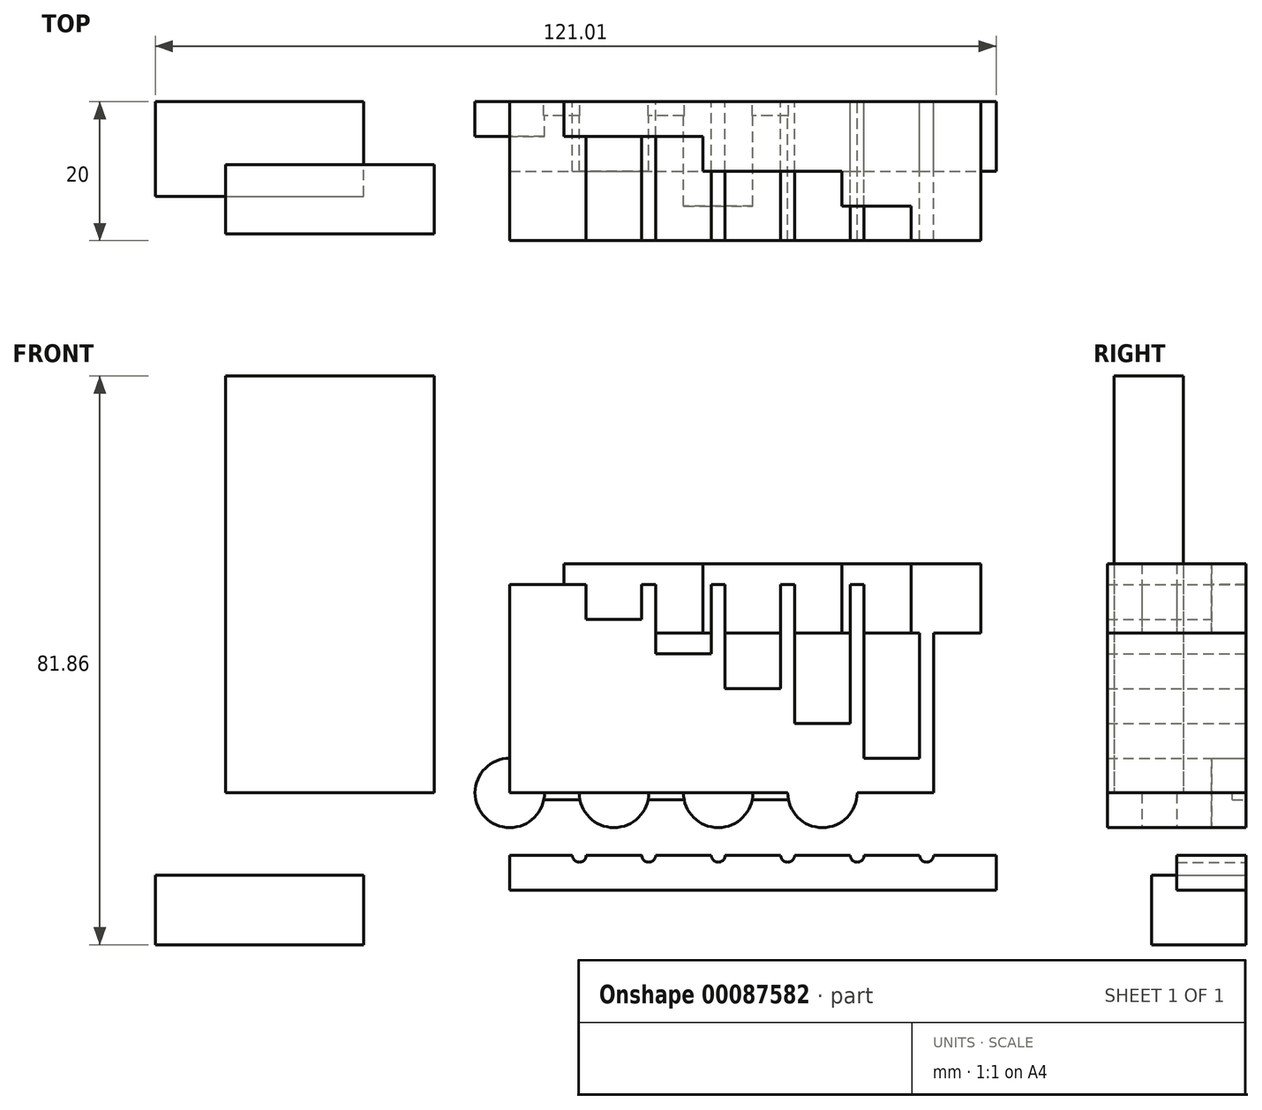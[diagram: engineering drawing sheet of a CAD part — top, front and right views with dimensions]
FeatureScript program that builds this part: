
annotation { "Feature Type Name" : "Feature", "Feature Type Description" : "" }
export const myFeature = defineFeature(function(context is Context, id is Id, definition is map)
    precondition{}
    {
        {
            var Q0;
            Q0=qCreatedBy(makeId("Front.planeOp"),FACE);
            var sketch = newSketch(context, id + "F0", { "sketchPlane" : qUnion([Q0])});
            skCircle(sketch, "E0", {"center": v(0, 0) * mm, "radius": 5 * mm});
            skCircle(sketch, "E1.1.0.0", {"center": v(15, 0) * mm, "radius": 5 * mm});
            skCircle(sketch, "E1.2.0.0", {"center": v(30, 0) * mm, "radius": 5 * mm});
            skCircle(sketch, "E1.3.0.0", {"center": v(45, 0) * mm, "radius": 5 * mm});
            skLineSegment(sketch, "E1.direction1", {"start": v(0, 0) * mm, "end": v(15, 0) * mm, "construction": true});
            skSolve(sketch);
        }
        {
            var Q0;
            Q0=makeQuery(id+"F0.imprint","IMPRINT",FACE,{"disambiguationData":[TD([[makeQuery(id+"F0.imprint","IMPRINT",EDGE,{"derivedFrom":sQuery(id+"F0.wireOp",EDGE,"E0")}),1.0]])]});
            extrude(context, id + "F1", {"entities" : qUnion([Q0]), "depth" : 5 * mm});
        }
        {
            var Q0;
            Q0=makeQuery(id+"F0.imprint","IMPRINT",FACE,{"disambiguationData":[TD([[makeQuery(id+"F0.imprint","IMPRINT",EDGE,{"derivedFrom":sQuery(id+"F0.wireOp",EDGE,"E1.1.0.0")}),1.0]])]});
            extrude(context, id + "F2", {"entities" : qUnion([Q0]), "depth" : 10 * mm});
        }
        {
            var Q0;
            Q0=makeQuery(id+"F0.imprint","IMPRINT",FACE,{"disambiguationData":[TD([[makeQuery(id+"F0.imprint","IMPRINT",EDGE,{"derivedFrom":sQuery(id+"F0.wireOp",EDGE,"E1.2.0.0")}),1.0]])]});
            extrude(context, id + "F3", {"entities" : qUnion([Q0]), "depth" : 15 * mm});
        }
        {
            var Q0;
            Q0=makeQuery(id+"F0.imprint","IMPRINT",FACE,{"disambiguationData":[TD([[makeQuery(id+"F0.imprint","IMPRINT",EDGE,{"derivedFrom":sQuery(id+"F0.wireOp",EDGE,"E1.3.0.0")}),1.0]])]});
            extrude(context, id + "F4", {"entities" : qUnion([Q0]), "depth" : 20 * mm});
        }
        {
            var Q0;
            Q0=makeQuery(id+"F0.imprint","IMPRINT",FACE,{"disambiguationData":[TD([[makeQuery(id+"F0.imprint","IMPRINT",EDGE,{"derivedFrom":sQuery(id+"F0.wireOp",EDGE,"E0")}),1.0]])]});
            var sketch = newSketch(context, id + "F5", { "sketchPlane" : qUnion([Q0])});
            skArc(sketch, "E2.0", {"start": v(45, -5) * mm, "mid": v(50, 0) * mm, "end": v(45, 5) * mm});
            skArc(sketch, "E2.1", {"start": v(0, 5) * mm, "mid": v(-5, 0) * mm, "end": v(0, -5) * mm});
            skLineSegment(sketch, "E3", {"start": v(45, -5) * mm, "end": v(0, -5) * mm});
            skLineSegment(sketch, "E4", {"start": v(0, 5) * mm, "end": v(45, 5) * mm});
            skSolve(sketch);
        }
        {
            var Q0;
            Q0=makeQuery(id+"F4.opExtrude","SWEPT_BODY",BODY,{"disambiguationData":[OSD([sQuery(id+"F0.wireOp",EDGE,"E1.3.0.0")])]});
            var Q1;
            Q1=makeQuery(id+"FrmGR7nz3px04QZ_4.opExtrude","SWEPT_BODY",BODY,{"disambiguationData":[OSD([sQuery(id+"F5.wireOp",EDGE,"E2.0"),sQuery(id+"F5.wireOp",EDGE,"E2.1"),sQuery(id+"F5.wireOp",EDGE,"E3"),sQuery(id+"F5.wireOp",EDGE,"E4")])]});
            var Q2;
            Q2=makeQuery(id+"F3.opExtrude","SWEPT_BODY",BODY,{"disambiguationData":[OSD([sQuery(id+"F0.wireOp",EDGE,"E1.2.0.0")])]});
            var Q3;
            Q3=makeQuery(id+"F2.opExtrude","SWEPT_BODY",BODY,{"disambiguationData":[OSD([sQuery(id+"F0.wireOp",EDGE,"E1.1.0.0")])]});
            var Q4;
            Q4=makeQuery(id+"F1.opExtrude","SWEPT_BODY",BODY,{"disambiguationData":[OSD([sQuery(id+"F0.wireOp",EDGE,"E0")])]});
            booleanBodies(context, id + "F6", {"operationType" : BooleanOperationType.UNION, "tools" : qUnion([Q0, Q1, Q2, Q3, Q4])});
        }
        {
            var Q0;
            Q0=makeQuery(id+"F6.opBoolean","MERGE",FACE,{"derivedFrom":[makeQuery(id+"F4.opExtrude","CAP_FACE",FACE,{"disambiguationData":[OSD([sQuery(id+"F0.wireOp",EDGE,"E1.3.0.0")])],"isStart":true}),makeQuery(id+"FrmGR7nz3px04QZ_4.opExtrude","CAP_FACE",FACE,{"disambiguationData":[OSD([sQuery(id+"F5.wireOp",EDGE,"E2.0"),sQuery(id+"F5.wireOp",EDGE,"E2.1"),sQuery(id+"F5.wireOp",EDGE,"E3"),sQuery(id+"F5.wireOp",EDGE,"E4")])],"isStart":true})]});
            var sketch = newSketch(context, id + "F7", { "sketchPlane" : qUnion([Q0])});
            skLineSegment(sketch, "E5.bottom", {"start": v(-67.8, 23) * mm, "end": v(-7.8, 23) * mm});
            skLineSegment(sketch, "E5.top", {"start": v(-67.8, 33) * mm, "end": v(-7.8, 33) * mm});
            skLineSegment(sketch, "E5.left", {"start": v(-67.8, 23) * mm, "end": v(-67.8, 33) * mm});
            skLineSegment(sketch, "E5.right", {"start": v(-7.8, 23) * mm, "end": v(-7.8, 33) * mm});
            skSolve(sketch);
        }
        {
            var Q0;
            Q0=makeQuery(id+"F7.imprint","IMPRINT",FACE,{"disambiguationData":[TD([[makeQuery(id+"F7.imprint","IMPRINT",EDGE,{"derivedFrom":sQuery(id+"F7.wireOp",EDGE,"E5.bottom")}),1.0]])]});
            extrude(context, id + "F8", {"entities" : qUnion([Q0]), "oppositeDirection" : true, "depth" : 5 * mm});
        }
        {
            var Q0;
            Q0=makeQuery(id+"F8.opExtrude","CAP_FACE",FACE,{"disambiguationData":[OSD([sQuery(id+"F7.wireOp",EDGE,"E5.bottom"),sQuery(id+"F7.wireOp",EDGE,"E5.top"),sQuery(id+"F7.wireOp",EDGE,"E5.left"),sQuery(id+"F7.wireOp",EDGE,"E5.right")])],"isStart":false});
            var sketch = newSketch(context, id + "F9", { "sketchPlane" : qUnion([Q0])});
            skLineSegment(sketch, "E6.bottom", {"start": v(67.8, 33) * mm, "end": v(27.8, 33) * mm});
            skLineSegment(sketch, "E6.top", {"start": v(67.8, 23) * mm, "end": v(27.8, 23) * mm});
            skLineSegment(sketch, "E6.left", {"start": v(67.8, 33) * mm, "end": v(67.8, 23) * mm});
            skLineSegment(sketch, "E6.right", {"start": v(27.8, 33) * mm, "end": v(27.8, 23) * mm});
            skSolve(sketch);
        }
        {
            var Q0;
            Q0=makeQuery(id+"F9.imprint","IMPRINT",FACE,{"disambiguationData":[TD([[makeQuery(id+"F9.imprint","IMPRINT",EDGE,{"derivedFrom":sQuery(id+"F9.wireOp",EDGE,"E6.bottom")}),1.0]])]});
            extrude(context, id + "F10", {"entities" : qUnion([Q0]), "operationType" : NewBodyOperationType.ADD, "depth" : 5 * mm});
        }
        {
            var Q0;
            Q0=makeQuery(id+"F10.opExtrude","CAP_FACE",FACE,{"disambiguationData":[OSD([sQuery(id+"F9.wireOp",EDGE,"E6.bottom"),sQuery(id+"F9.wireOp",EDGE,"E6.top"),sQuery(id+"F9.wireOp",EDGE,"E6.left"),sQuery(id+"F9.wireOp",EDGE,"E6.right")])],"isStart":false});
            var sketch = newSketch(context, id + "F11", { "sketchPlane" : qUnion([Q0])});
            skLineSegment(sketch, "E7.bottom", {"start": v(67.8, 33) * mm, "end": v(47.8, 33) * mm});
            skLineSegment(sketch, "E7.top", {"start": v(67.8, 23) * mm, "end": v(47.8, 23) * mm});
            skLineSegment(sketch, "E7.left", {"start": v(67.8, 33) * mm, "end": v(67.8, 23) * mm});
            skLineSegment(sketch, "E7.right", {"start": v(47.8, 33) * mm, "end": v(47.8, 23) * mm});
            skSolve(sketch);
        }
        {
            var Q0;
            Q0=makeQuery(id+"F11.imprint","IMPRINT",FACE,{"disambiguationData":[TD([[makeQuery(id+"F11.imprint","IMPRINT",EDGE,{"derivedFrom":sQuery(id+"F11.wireOp",EDGE,"E7.bottom")}),1.0]])]});
            extrude(context, id + "F12", {"entities" : qUnion([Q0]), "operationType" : NewBodyOperationType.ADD, "depth" : 5 * mm});
        }
        {
            var Q0;
            Q0=makeQuery(id+"F12.opExtrude","CAP_FACE",FACE,{"disambiguationData":[OSD([sQuery(id+"F11.wireOp",EDGE,"E7.bottom"),sQuery(id+"F11.wireOp",EDGE,"E7.top"),sQuery(id+"F11.wireOp",EDGE,"E7.left"),sQuery(id+"F11.wireOp",EDGE,"E7.right")])],"isStart":false});
            var sketch = newSketch(context, id + "F13", { "sketchPlane" : qUnion([Q0])});
            skLineSegment(sketch, "E8.bottom", {"start": v(67.8, 33) * mm, "end": v(57.8, 33) * mm});
            skLineSegment(sketch, "E8.top", {"start": v(67.8, 23) * mm, "end": v(57.8, 23) * mm});
            skLineSegment(sketch, "E8.left", {"start": v(67.8, 33) * mm, "end": v(67.8, 23) * mm});
            skLineSegment(sketch, "E8.right", {"start": v(57.8, 33) * mm, "end": v(57.8, 23) * mm});
            skSolve(sketch);
        }
        {
            var Q0;
            Q0=makeQuery(id+"F13.imprint","IMPRINT",FACE,{"disambiguationData":[TD([[makeQuery(id+"F13.imprint","IMPRINT",EDGE,{"derivedFrom":sQuery(id+"F13.wireOp",EDGE,"E8.bottom")}),1.0]])]});
            extrude(context, id + "F14", {"entities" : qUnion([Q0]), "operationType" : NewBodyOperationType.ADD, "depth" : 5 * mm});
        }
        {
            var Q0;
            {var subQ0=sQuery(id+"F5.wireOp",EDGE,"E2.1");Q0=makeQuery(id+"F5.imprint","IMPRINT",FACE,{"disambiguationData":[TD([[makeQuery(id+"F5.imprint","IMPRINT",EDGE,{"derivedFrom":subQ0}),1.0]])]});}
            var sketch = newSketch(context, id + "F15", { "sketchPlane" : qUnion([Q0])});
            skLineSegment(sketch, "E9.bottom", {"start": v(45.2, -1) * mm, "end": v(0.29, -1) * mm});
            skLineSegment(sketch, "E9.top", {"start": v(45.2, 1) * mm, "end": v(0.29, 1) * mm});
            skLineSegment(sketch, "E9.left", {"start": v(45.2, -1) * mm, "end": v(45.2, 1) * mm});
            skLineSegment(sketch, "E9.right", {"start": v(0.29, -1) * mm, "end": v(0.29, 1) * mm});
            skPoint(sketch, "E9.middle", {"position": v(22.75, 0) * mm});
            skSolve(sketch);
        }
        {
            var Q0;
            Q0 = qSketchRegion(id + "F15", true);
            extrude(context, id + "F16", {"entities" : qUnion([Q0]), "operationType" : NewBodyOperationType.ADD, "depth" : 2 * mm});
        }
        {
            var Q0;
            Q0=qCreatedBy(makeId("Top.planeOp"),FACE);
            var sketch = newSketch(context, id + "F17", { "sketchPlane" : qUnion([Q0])});
            skLineSegment(sketch, "E10.bottom", {"start": v(-40.9, -9.03) * mm, "end": v(-10.9, -9.03) * mm});
            skLineSegment(sketch, "E10.top", {"start": v(-40.9, -19.03) * mm, "end": v(-10.9, -19.03) * mm});
            skLineSegment(sketch, "E10.left", {"start": v(-40.9, -9.03) * mm, "end": v(-40.9, -19.03) * mm});
            skLineSegment(sketch, "E10.right", {"start": v(-10.9, -9.03) * mm, "end": v(-10.9, -19.03) * mm});
            skSolve(sketch);
        }
        {
            var Q0;
            Q0=makeQuery(id+"F17.imprint","IMPRINT",FACE,{"disambiguationData":[TD([[makeQuery(id+"F17.imprint","IMPRINT",EDGE,{"derivedFrom":sQuery(id+"F17.wireOp",EDGE,"E10.bottom")}),-1.0]])]});
            extrude(context, id + "F18", {"entities" : qUnion([Q0]), "depth" : 60 * mm});
        }
        {
            var Q0;
            Q0=qCreatedBy(makeId("Front.planeOp"),FACE);
            var sketch = newSketch(context, id + "F19", { "sketchPlane" : qUnion([Q0])});
            skLineSegment(sketch, "E11", {"start": v(0, 0) * mm, "end": v(60, 0) * mm});
            skLineSegment(sketch, "E12", {"start": v(60, 0) * mm, "end": v(60, 5) * mm});
            skLineSegment(sketch, "E13", {"start": v(60, 5) * mm, "end": v(50, 5) * mm});
            skLineSegment(sketch, "E14", {"start": v(50, 5) * mm, "end": v(50, 10) * mm});
            skLineSegment(sketch, "E15", {"start": v(50, 10) * mm, "end": v(40, 10) * mm});
            skLineSegment(sketch, "E16", {"start": v(40, 10) * mm, "end": v(40, 15) * mm});
            skLineSegment(sketch, "E17", {"start": v(40, 15) * mm, "end": v(30, 15) * mm});
            skLineSegment(sketch, "E18", {"start": v(30, 15) * mm, "end": v(30, 20) * mm});
            skLineSegment(sketch, "E19", {"start": v(30, 20) * mm, "end": v(20, 20) * mm});
            skLineSegment(sketch, "E20", {"start": v(20, 20) * mm, "end": v(20, 25) * mm});
            skLineSegment(sketch, "E21", {"start": v(20, 25) * mm, "end": v(10, 25) * mm});
            skLineSegment(sketch, "E22", {"start": v(10, 25) * mm, "end": v(10, 30) * mm});
            skLineSegment(sketch, "E23", {"start": v(10, 30) * mm, "end": v(0, 30) * mm});
            skLineSegment(sketch, "E24", {"start": v(0, 30) * mm, "end": v(0, 0) * mm});
            skLineSegment(sketch, "E25.bottom", {"start": v(0, -8.98) * mm, "end": v(9, -8.98) * mm});
            skLineSegment(sketch, "E25.top", {"start": v(0, -13.98) * mm, "end": v(70, -13.98) * mm});
            skLineSegment(sketch, "E25.left", {"start": v(0, -8.98) * mm, "end": v(0, -13.98) * mm});
            skLineSegment(sketch, "E25.right", {"start": v(70, -8.98) * mm, "end": v(70, -13.98) * mm});
            skArc(sketch, "E26", {"start": v(9, -8.98) * mm, "mid": v(10, -9.98) * mm, "end": v(11, -8.98) * mm});
            skArc(sketch, "E27.1.0.0", {"start": v(19, -8.98) * mm, "mid": v(20, -9.98) * mm, "end": v(21, -8.98) * mm});
            skArc(sketch, "E27.2.0.0", {"start": v(29, -8.98) * mm, "mid": v(30, -9.98) * mm, "end": v(31, -8.98) * mm});
            skArc(sketch, "E27.3.0.0", {"start": v(39, -8.98) * mm, "mid": v(40, -9.98) * mm, "end": v(41, -8.98) * mm});
            skArc(sketch, "E27.4.0.0", {"start": v(49, -8.98) * mm, "mid": v(50, -9.98) * mm, "end": v(51, -8.98) * mm});
            skArc(sketch, "E27.5.0.0", {"start": v(59, -8.98) * mm, "mid": v(60, -9.98) * mm, "end": v(61, -8.98) * mm});
            skLineSegment(sketch, "E27.direction1", {"start": v(11, -8.98) * mm, "end": v(19, -8.98) * mm, "construction": true});
            skLineSegment(sketch, "E28", {"start": v(10, 25) * mm, "end": v(10, -8.98) * mm, "construction": true});
            skLineSegment(sketch, "E29.trimOffspring", {"start": v(11, -8.98) * mm, "end": v(19, -8.98) * mm});
            skLineSegment(sketch, "E30.trimOffspring", {"start": v(21, -8.98) * mm, "end": v(29, -8.98) * mm});
            skLineSegment(sketch, "E31.trimOffspring", {"start": v(31, -8.98) * mm, "end": v(39, -8.98) * mm});
            skLineSegment(sketch, "E32.trimOffspring", {"start": v(41, -8.98) * mm, "end": v(49, -8.98) * mm});
            skLineSegment(sketch, "E33.trimOffspring", {"start": v(51, -8.98) * mm, "end": v(59, -8.98) * mm});
            skLineSegment(sketch, "E34.trimOffspring", {"start": v(61, -8.98) * mm, "end": v(70, -8.98) * mm});
            skLineSegment(sketch, "E35.bottom", {"start": v(11, 0) * mm, "end": v(9, 0) * mm});
            skLineSegment(sketch, "E35.top", {"start": v(11, 30) * mm, "end": v(9, 30) * mm});
            skLineSegment(sketch, "E35.left", {"start": v(11, 0) * mm, "end": v(11, 30) * mm});
            skLineSegment(sketch, "E35.right", {"start": v(9, 0) * mm, "end": v(9, 30) * mm});
            skLineSegment(sketch, "E36.1.0.0", {"start": v(21, 0) * mm, "end": v(21, 30) * mm});
            skLineSegment(sketch, "E36.1.0.1", {"start": v(21, 30) * mm, "end": v(19, 30) * mm});
            skLineSegment(sketch, "E36.1.0.2", {"start": v(19, 0) * mm, "end": v(19, 30) * mm});
            skLineSegment(sketch, "E36.2.0.0", {"start": v(31, 0) * mm, "end": v(31, 30) * mm});
            skLineSegment(sketch, "E36.2.0.1", {"start": v(31, 30) * mm, "end": v(29, 30) * mm});
            skLineSegment(sketch, "E36.2.0.2", {"start": v(29, 0) * mm, "end": v(29, 30) * mm});
            skLineSegment(sketch, "E36.3.0.0", {"start": v(41, 0) * mm, "end": v(41, 30) * mm});
            skLineSegment(sketch, "E36.3.0.1", {"start": v(41, 30) * mm, "end": v(39, 30) * mm});
            skLineSegment(sketch, "E36.3.0.2", {"start": v(39, 0) * mm, "end": v(39, 30) * mm});
            skLineSegment(sketch, "E36.4.0.0", {"start": v(51, 0) * mm, "end": v(51, 30) * mm});
            skLineSegment(sketch, "E36.4.0.1", {"start": v(51, 30) * mm, "end": v(49, 30) * mm});
            skLineSegment(sketch, "E36.4.0.2", {"start": v(49, 0) * mm, "end": v(49, 30) * mm});
            skLineSegment(sketch, "E36.5.0.0", {"start": v(61, 0) * mm, "end": v(61, 30) * mm});
            skLineSegment(sketch, "E36.5.0.1", {"start": v(61, 30) * mm, "end": v(59, 30) * mm});
            skLineSegment(sketch, "E36.5.0.2", {"start": v(59, 0) * mm, "end": v(59, 30) * mm});
            skLineSegment(sketch, "E36.direction1", {"start": v(9, 0) * mm, "end": v(19, 0) * mm, "construction": true});
            skLineSegment(sketch, "E37", {"start": v(61, 0) * mm, "end": v(60, 0) * mm});
            skSolve(sketch);
        }
        {
            var Q0;
            Q0 = qSketchRegion(id + "F19", true);
            extrude(context, id + "F20", {"entities" : qUnion([Q0]), "depth" : 10 * mm});
        }
        {
            var Q0;
            Q0=makeQuery(id+"F20.opExtrude","CAP_FACE",FACE,{"disambiguationData":[OSD([sQuery(id+"F19.wireOp",EDGE,"E11"),sQuery(id+"F19.wireOp",EDGE,"E13"),sQuery(id+"F19.wireOp",EDGE,"E15"),sQuery(id+"F19.wireOp",EDGE,"E17"),sQuery(id+"F19.wireOp",EDGE,"E19"),sQuery(id+"F19.wireOp",EDGE,"E21"),sQuery(id+"F19.wireOp",EDGE,"E23"),sQuery(id+"F19.wireOp",EDGE,"E24"),sQuery(id+"F19.wireOp",EDGE,"E35.bottom"),sQuery(id+"F19.wireOp",EDGE,"E35.top"),sQuery(id+"F19.wireOp",EDGE,"E35.left"),sQuery(id+"F19.wireOp",EDGE,"E36.1.0.0"),sQuery(id+"F19.wireOp",EDGE,"E36.1.0.1"),sQuery(id+"F19.wireOp",EDGE,"E36.1.0.2"),sQuery(id+"F19.wireOp",EDGE,"E36.2.0.0"),sQuery(id+"F19.wireOp",EDGE,"E36.2.0.1"),sQuery(id+"F19.wireOp",EDGE,"E36.2.0.2"),sQuery(id+"F19.wireOp",EDGE,"E36.3.0.0"),sQuery(id+"F19.wireOp",EDGE,"E36.3.0.1"),sQuery(id+"F19.wireOp",EDGE,"E36.3.0.2"),sQuery(id+"F19.wireOp",EDGE,"E36.4.0.0"),sQuery(id+"F19.wireOp",EDGE,"E36.4.0.1"),sQuery(id+"F19.wireOp",EDGE,"E36.4.0.2"),sQuery(id+"F19.wireOp",EDGE,"E36.5.0.0"),sQuery(id+"F19.wireOp",EDGE,"E36.5.0.1"),sQuery(id+"F19.wireOp",EDGE,"E36.5.0.2"),sQuery(id+"F19.wireOp",EDGE,"E37")])],"isStart":false});
            extrude(context, id + "F21", {"entities" : qUnion([Q0]), "operationType" : NewBodyOperationType.ADD, "depth" : 10 * mm});
        }
        {
            var Q0;
            Q0=qCreatedBy(makeId("Front.planeOp"),FACE);
            var sketch = newSketch(context, id + "F22", { "sketchPlane" : qUnion([Q0])});
            skLineSegment(sketch, "E38.bottom", {"start": v(-51, -11.86) * mm, "end": v(-21, -11.86) * mm});
            skLineSegment(sketch, "E38.top", {"start": v(-51, -21.86) * mm, "end": v(-21, -21.86) * mm});
            skLineSegment(sketch, "E38.left", {"start": v(-51, -11.86) * mm, "end": v(-51, -21.86) * mm});
            skLineSegment(sketch, "E38.right", {"start": v(-21, -11.86) * mm, "end": v(-21, -21.86) * mm});
            skSolve(sketch);
        }
        {
            var Q0;
            Q0=makeQuery(id+"F22.imprint","IMPRINT",FACE,{"disambiguationData":[TD([[makeQuery(id+"F22.imprint","IMPRINT",EDGE,{"derivedFrom":sQuery(id+"F22.wireOp",EDGE,"E38.bottom")}),-1.0]])]});
            extrude(context, id + "F23", {"entities" : qUnion([Q0]), "depth" : 13.6 * mm});
        }
    });
